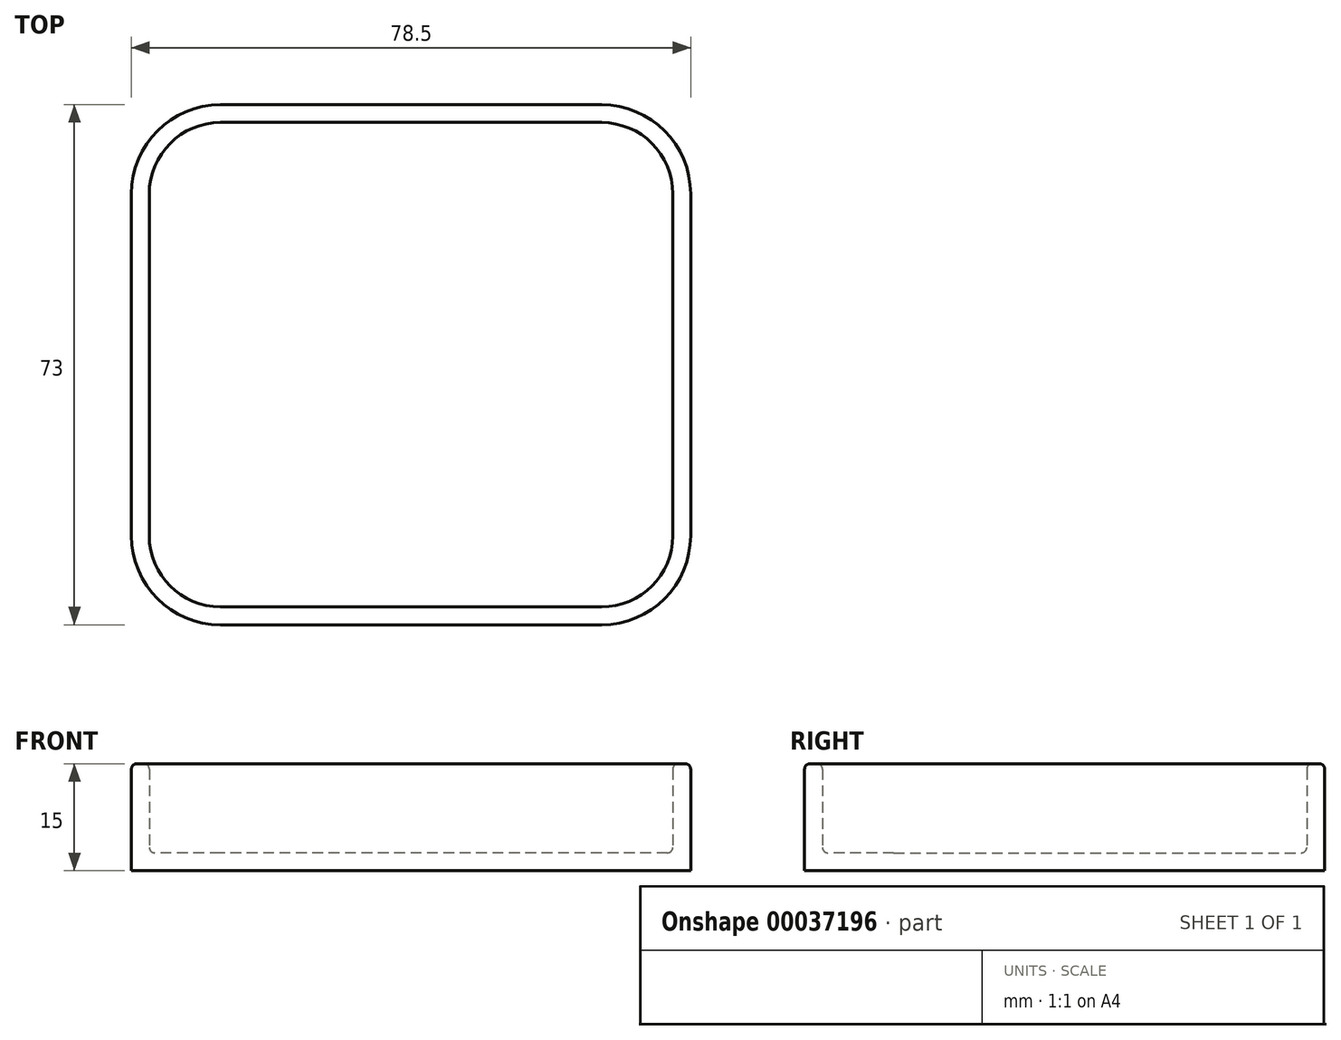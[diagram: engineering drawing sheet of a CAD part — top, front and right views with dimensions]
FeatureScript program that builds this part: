
annotation { "Feature Type Name" : "Feature", "Feature Type Description" : "" }
export const myFeature = defineFeature(function(context is Context, id is Id, definition is map)
    precondition{}
    {
        {
            var Q0;
            Q0=qCreatedBy(makeId("Top.planeOp"),FACE);
            var sketch = newSketch(context, id + "F0", { "sketchPlane" : qUnion([Q0])});
            skLineSegment(sketch, "E0.bottom", {"start": v(-26.75, 36.5) * mm, "end": v(26.75, 36.5) * mm});
            skLineSegment(sketch, "E0.top", {"start": v(-26.75, -36.5) * mm, "end": v(26.75, -36.5) * mm});
            skLineSegment(sketch, "E0.left", {"start": v(-39.25, 24) * mm, "end": v(-39.25, -24) * mm});
            skLineSegment(sketch, "E0.right", {"start": v(39.25, 24) * mm, "end": v(39.25, -24) * mm});
            skPoint(sketch, "E0.middle", {"position": v(0, 0) * mm});
            skLineSegment(sketch, "E1.bottom", {"start": v(-26.75, 34) * mm, "end": v(26.75, 34) * mm});
            skLineSegment(sketch, "E1.top", {"start": v(-26.75, -34) * mm, "end": v(26.75, -34) * mm});
            skLineSegment(sketch, "E1.left", {"start": v(-36.75, 24) * mm, "end": v(-36.75, -24) * mm});
            skLineSegment(sketch, "E1.right", {"start": v(36.75, 24) * mm, "end": v(36.75, -24) * mm});
            skPoint(sketch, "E2.visualSharp", {"position": v(-36.75, 34) * mm});
            skArc(sketch, "E2.filletArc", {"start": v(-26.75, 34) * mm, "mid": v(-33.82, 31.07) * mm, "end": v(-36.75, 24) * mm});
            skPoint(sketch, "E3.visualSharp", {"position": v(36.75, 34) * mm});
            skArc(sketch, "E3.filletArc", {"start": v(36.75, 24) * mm, "mid": v(33.82, 31.07) * mm, "end": v(26.75, 34) * mm});
            skPoint(sketch, "E4.visualSharp", {"position": v(-36.75, -34) * mm});
            skArc(sketch, "E4.filletArc", {"start": v(-36.75, -24) * mm, "mid": v(-33.82, -31.07) * mm, "end": v(-26.75, -34) * mm});
            skPoint(sketch, "E5.visualSharp", {"position": v(36.75, -34) * mm});
            skArc(sketch, "E5.filletArc", {"start": v(26.75, -34) * mm, "mid": v(33.82, -31.07) * mm, "end": v(36.75, -24) * mm});
            skPoint(sketch, "E6.visualSharp", {"position": v(-39.25, 36.5) * mm});
            skArc(sketch, "E6.filletArc", {"start": v(-26.75, 36.5) * mm, "mid": v(-35.59, 32.84) * mm, "end": v(-39.25, 24) * mm});
            skPoint(sketch, "E7.visualSharp", {"position": v(-39.25, -36.5) * mm});
            skArc(sketch, "E7.filletArc", {"start": v(-39.25, -24) * mm, "mid": v(-35.59, -32.84) * mm, "end": v(-26.75, -36.5) * mm});
            skPoint(sketch, "E8.visualSharp", {"position": v(39.25, -36.5) * mm});
            skArc(sketch, "E8.filletArc", {"start": v(26.75, -36.5) * mm, "mid": v(35.59, -32.84) * mm, "end": v(39.25, -24) * mm});
            skPoint(sketch, "E9.visualSharp", {"position": v(39.25, 36.5) * mm});
            skArc(sketch, "E9.filletArc", {"start": v(39.25, 24) * mm, "mid": v(35.59, 32.84) * mm, "end": v(26.75, 36.5) * mm});
            skSolve(sketch);
        }
        {
            var Q0;
            Q0 = qSketchRegion(id + "F0", true);
            var Q1;
            Q1=makeQuery(id+"F0.imprint","IMPRINT",FACE,{"disambiguationData":[TD([[makeQuery(id+"F0.imprint","IMPRINT",EDGE,{"derivedFrom":sQuery(id+"F0.wireOp",EDGE,"E1.bottom")}),-1.0]])]});
            extrude(context, id + "F1", {"entities" : qUnion([Q0, Q1]), "depth" : 2.5 * mm, "offsetDistance" : 25 * mm});
        }
        {
            var Q0;
            Q0 = qSketchRegion(id + "F0", true);
            extrude(context, id + "F2", {"entities" : qUnion([Q0]), "operationType" : NewBodyOperationType.ADD, "depth" : 15 * mm, "offsetDistance" : 25 * mm});
        }
        {
            var Q0;
            Q0=makeQuery(id+"F2.opExtrude","CAP_FACE",FACE,{"disambiguationData":[OSD([sQuery(id+"F0.wireOp",EDGE,"E0.bottom"),sQuery(id+"F0.wireOp",EDGE,"E0.top"),sQuery(id+"F0.wireOp",EDGE,"E0.left"),sQuery(id+"F0.wireOp",EDGE,"E0.right"),sQuery(id+"F0.wireOp",EDGE,"E1.bottom"),sQuery(id+"F0.wireOp",EDGE,"E1.top"),sQuery(id+"F0.wireOp",EDGE,"E1.left"),sQuery(id+"F0.wireOp",EDGE,"E1.right"),sQuery(id+"F0.wireOp",EDGE,"E2.filletArc"),sQuery(id+"F0.wireOp",EDGE,"E3.filletArc"),sQuery(id+"F0.wireOp",EDGE,"E4.filletArc"),sQuery(id+"F0.wireOp",EDGE,"E5.filletArc"),sQuery(id+"F0.wireOp",EDGE,"E6.filletArc"),sQuery(id+"F0.wireOp",EDGE,"E7.filletArc"),sQuery(id+"F0.wireOp",EDGE,"E8.filletArc"),sQuery(id+"F0.wireOp",EDGE,"E9.filletArc")])],"isStart":false});
            var Q1;
            Q1=makeQuery(id+"F1.opExtrude","CAP_FACE",FACE,{"disambiguationData":[OSD([sQuery(id+"F0.wireOp",EDGE,"E0.bottom"),sQuery(id+"F0.wireOp",EDGE,"E0.top"),sQuery(id+"F0.wireOp",EDGE,"E0.left"),sQuery(id+"F0.wireOp",EDGE,"E0.right"),sQuery(id+"F0.wireOp",EDGE,"E6.filletArc"),sQuery(id+"F0.wireOp",EDGE,"E7.filletArc"),sQuery(id+"F0.wireOp",EDGE,"E8.filletArc"),sQuery(id+"F0.wireOp",EDGE,"E9.filletArc")])],"isStart":false});
            fillet(context, id + "F3", {"entities" : qUnion([Q0, Q1]), "radius" : .75 * mm, "tangentPropagation" : true, "allowEdgeOverflow" : false});
        }
    });
